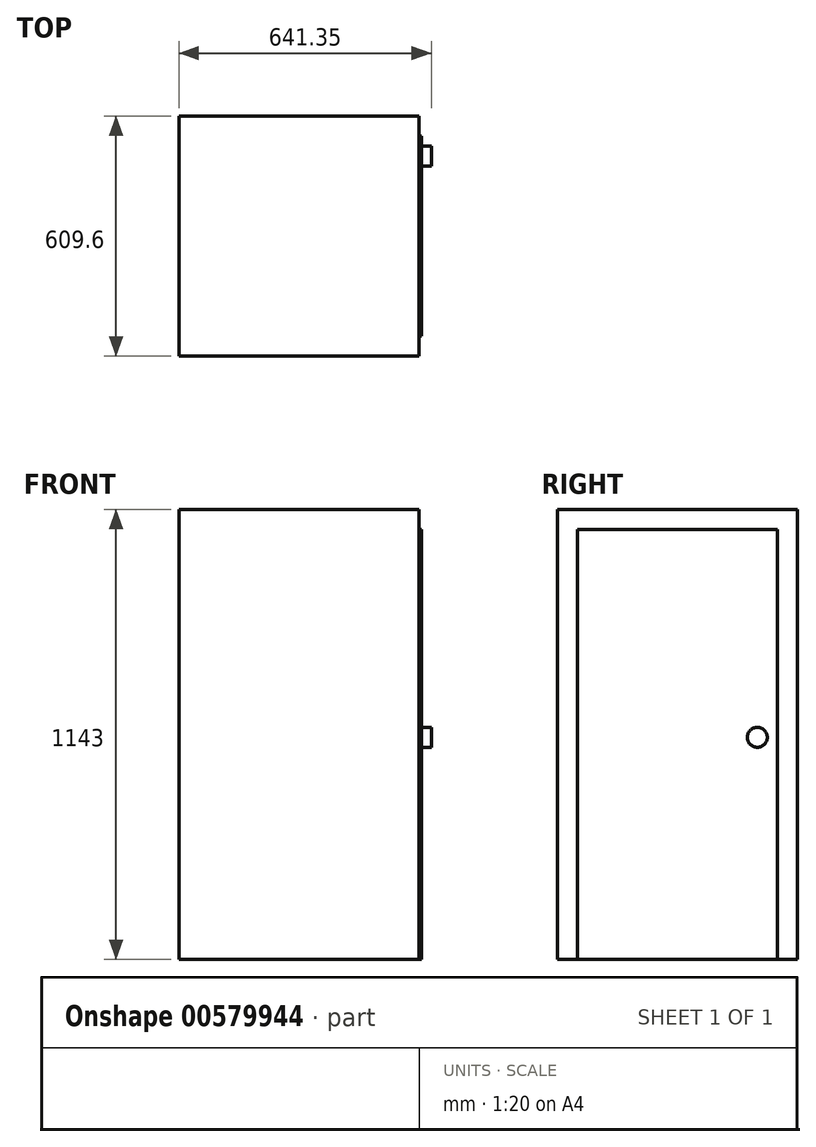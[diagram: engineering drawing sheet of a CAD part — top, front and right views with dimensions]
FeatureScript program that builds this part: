
annotation { "Feature Type Name" : "Feature", "Feature Type Description" : "" }
export const myFeature = defineFeature(function(context is Context, id is Id, definition is map)
    precondition{}
    {
        {
            var Q0;
            Q0=qCreatedBy(makeId("Right.planeOp"),FACE);
            var sketch = newSketch(context, id + "F0", { "sketchPlane" : qUnion([Q0])});
            skLineSegment(sketch, "E0.bottom", {"start": v(-380.8, 578.86) * mm, "end": v(228.8, 578.86) * mm});
            skLineSegment(sketch, "E0.top", {"start": v(-380.8, -564.14) * mm, "end": v(228.8, -564.14) * mm});
            skLineSegment(sketch, "E0.left", {"start": v(-380.8, 578.86) * mm, "end": v(-380.8, -564.14) * mm});
            skLineSegment(sketch, "E0.right", {"start": v(228.8, 578.86) * mm, "end": v(228.8, -564.14) * mm});
            skSolve(sketch);
        }
        {
            var Q0;
            Q0=makeQuery(id+"F0.imprint","IMPRINT",FACE,{"disambiguationData":[TD([[makeQuery(id+"F0.imprint","IMPRINT",EDGE,{"derivedFrom":sQuery(id+"F0.wireOp",EDGE,"E0.bottom")}),-1.0]])]});
            extrude(context, id + "F1", {"entities" : qUnion([Q0]), "depth" : 609.6 * mm, "offsetDistance" : 25.4 * mm});
        }
        {
            var Q0;
            Q0=makeQuery(id+"F1.opExtrude","CAP_FACE",FACE,{"disambiguationData":[OSD([sQuery(id+"F0.wireOp",EDGE,"E0.bottom"),sQuery(id+"F0.wireOp",EDGE,"E0.top"),sQuery(id+"F0.wireOp",EDGE,"E0.left"),sQuery(id+"F0.wireOp",EDGE,"E0.right")])],"isStart":false});
            var sketch = newSketch(context, id + "F2", { "sketchPlane" : qUnion([Q0])});
            skLineSegment(sketch, "E1.bottom", {"start": v(-330, -564.14) * mm, "end": v(178, -564.14) * mm});
            skLineSegment(sketch, "E1.top", {"start": v(-330, 528.06) * mm, "end": v(178, 528.06) * mm});
            skLineSegment(sketch, "E1.left", {"start": v(-330, -564.14) * mm, "end": v(-330, 528.06) * mm});
            skLineSegment(sketch, "E1.right", {"start": v(178, -564.14) * mm, "end": v(178, 528.06) * mm});
            skSolve(sketch);
        }
        {
            var Q0;
            Q0=makeQuery(id+"F2.imprint","IMPRINT",FACE,{"disambiguationData":[TD([[makeQuery(id+"F2.imprint","IMPRINT",EDGE,{"derivedFrom":sQuery(id+"F2.wireOp",EDGE,"E1.bottom")}),1.0]])]});
            extrude(context, id + "F3", {"entities" : qUnion([Q0]), "operationType" : NewBodyOperationType.ADD, "depth" : 6.35 * mm, "offsetDistance" : 25.4 * mm});
        }
        {
            var Q0;
            Q0=makeQuery(id+"F3.opExtrude","CAP_FACE",FACE,{"disambiguationData":[OSD([sQuery(id+"F2.wireOp",EDGE,"E1.bottom"),sQuery(id+"F2.wireOp",EDGE,"E1.top"),sQuery(id+"F2.wireOp",EDGE,"E1.left"),sQuery(id+"F2.wireOp",EDGE,"E1.right")])],"isStart":false});
            var sketch = newSketch(context, id + "F4", { "sketchPlane" : qUnion([Q0])});
            skCircle(sketch, "E2", {"center": v(127.2, 0) * mm, "radius": 25.4 * mm});
            skSolve(sketch);
        }
        {
            var Q0;
            Q0=makeQuery(id+"F4.imprint","IMPRINT",FACE,{"disambiguationData":[TD([[makeQuery(id+"F4.imprint","IMPRINT",EDGE,{"derivedFrom":sQuery(id+"F4.wireOp",EDGE,"E2")}),1.0]])]});
            extrude(context, id + "F5", {"entities" : qUnion([Q0]), "operationType" : NewBodyOperationType.ADD, "depth" : 25.4 * mm, "offsetDistance" : 25.4 * mm});
        }
    });
